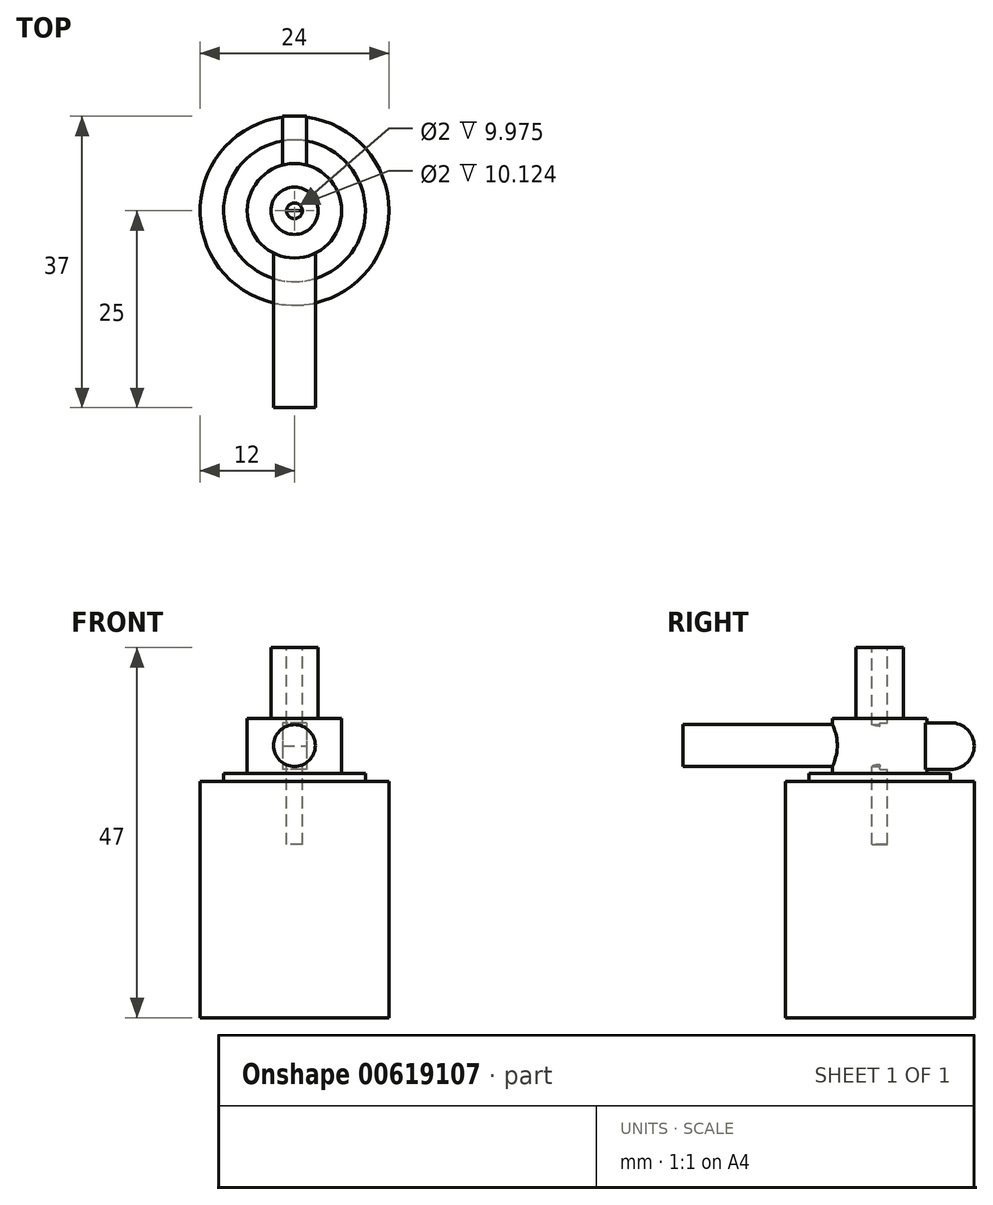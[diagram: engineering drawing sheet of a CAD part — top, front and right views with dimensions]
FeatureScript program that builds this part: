
annotation { "Feature Type Name" : "Feature", "Feature Type Description" : "" }
export const myFeature = defineFeature(function(context is Context, id is Id, definition is map)
    precondition{}
    {
        {
            var Q0;
            Q0=qCreatedBy(makeId("Top.planeOp"),FACE);
            var sketch = newSketch(context, id + "F0", { "sketchPlane" : qUnion([Q0])});
            skCircle(sketch, "E0", {"center": v(0, 0) * mm, "radius": 12 * mm});
            skSolve(sketch);
        }
        {
            var Q0;
            Q0 = qSketchRegion(id + "F0", true);
            extrude(context, id + "F1", {"entities" : qUnion([Q0]), "depth" : 30 * mm, "offsetDistance" : 25 * mm});
        }
        {
            var Q0;
            Q0=makeQuery(id+"F1.opExtrude","CAP_FACE",FACE,{"disambiguationData":[OSD([sQuery(id+"F0.wireOp",EDGE,"E0")])],"isStart":false});
            var sketch = newSketch(context, id + "F2", { "sketchPlane" : qUnion([Q0])});
            skCircle(sketch, "E1", {"center": v(0, 0) * mm, "radius": 9 * mm});
            skSolve(sketch);
        }
        {
            var Q0;
            Q0 = qSketchRegion(id + "F2", true);
            extrude(context, id + "F3", {"entities" : qUnion([Q0]), "operationType" : NewBodyOperationType.ADD, "depth" : 1 * mm, "offsetDistance" : 25 * mm});
        }
        {
            var Q0;
            Q0=makeQuery(id+"F3.opExtrude","CAP_FACE",FACE,{"disambiguationData":[OSD([sQuery(id+"F2.wireOp",EDGE,"E1")])],"isStart":false});
            var sketch = newSketch(context, id + "F4", { "sketchPlane" : qUnion([Q0])});
            skCircle(sketch, "E2", {"center": v(0, 0) * mm, "radius": 6 * mm});
            skSolve(sketch);
        }
        {
            var Q0;
            Q0 = qSketchRegion(id + "F4", true);
            extrude(context, id + "F5", {"entities" : qUnion([Q0]), "operationType" : NewBodyOperationType.ADD, "depth" : 7 * mm, "offsetDistance" : 25 * mm});
        }
        {
            var Q0;
            Q0=makeQuery(id+"F5.opExtrude","CAP_FACE",FACE,{"disambiguationData":[OSD([sQuery(id+"F4.wireOp",EDGE,"E2")])],"isStart":false});
            var sketch = newSketch(context, id + "F6", { "sketchPlane" : qUnion([Q0])});
            skCircle(sketch, "E3", {"center": v(0, 0) * mm, "radius": 3 * mm});
            skSolve(sketch);
        }
        {
            var Q0;
            Q0 = qSketchRegion(id + "F6", true);
            extrude(context, id + "F7", {"entities" : qUnion([Q0]), "operationType" : NewBodyOperationType.ADD, "depth" : 9 * mm, "offsetDistance" : 25 * mm});
        }
        {
            var Q0;
            Q0=makeQuery(id+"F7.opExtrude","CAP_FACE",FACE,{"disambiguationData":[OSD([sQuery(id+"F6.wireOp",EDGE,"E3")])],"isStart":false});
            var sketch = newSketch(context, id + "F8", { "sketchPlane" : qUnion([Q0])});
            skCircle(sketch, "E4", {"center": v(0, 0) * mm, "radius": 1 * mm});
            skSolve(sketch);
        }
        {
            var Q0;
            Q0 = qSketchRegion(id + "F8", true);
            extrude(context, id + "F9", {"entities" : qUnion([Q0]), "operationType" : NewBodyOperationType.REMOVE, "oppositeDirection" : true, "depth" : 25 * mm, "offsetDistance" : 25 * mm});
        }
        {
            var Q0;
            Q0=qCreatedBy(makeId("Front.planeOp"),FACE);
            var sketch = newSketch(context, id + "F10", { "sketchPlane" : qUnion([Q0])});
            skCircle(sketch, "E5", {"center": v(0, 34.57) * mm, "radius": 2.65 * mm});
            skSolve(sketch);
        }
        {
            var Q0;
            Q0 = qSketchRegion(id + "F10", true);
            extrude(context, id + "F11", {"entities" : qUnion([Q0]), "operationType" : NewBodyOperationType.ADD, "depth" : 25 * mm, "offsetDistance" : 25 * mm});
        }
        {
            var Q0;
            Q0=qCreatedBy(makeId("Front.planeOp"),FACE);
            var sketch = newSketch(context, id + "F12", { "sketchPlane" : qUnion([Q0])});
            skLineSegment(sketch, "E6.bottom", {"start": v(1.5, 37.47) * mm, "end": v(-1.5, 37.47) * mm});
            skLineSegment(sketch, "E6.top", {"start": v(1.5, 31.55) * mm, "end": v(-1.5, 31.55) * mm});
            skLineSegment(sketch, "E6.left", {"start": v(1.5, 37.47) * mm, "end": v(1.5, 31.55) * mm});
            skLineSegment(sketch, "E6.right", {"start": v(-1.5, 37.47) * mm, "end": v(-1.5, 31.55) * mm});
            skSolve(sketch);
        }
        {
            var Q0;
            Q0 = qSketchRegion(id + "F12", true);
            extrude(context, id + "F13", {"entities" : qUnion([Q0]), "operationType" : NewBodyOperationType.ADD, "oppositeDirection" : true, "depth" : 12 * mm, "offsetDistance" : 25 * mm});
        }
        {
            var Q0;
            Q0=makeQuery(id+"F13.opExtrude","CAP_EDGE",EDGE,{"disambiguationData":[OSD([sQuery(id+"F12.wireOp",EDGE,"E6.bottom")])],"isStart":false});
            var Q1;
            Q1=makeQuery(id+"F13.opExtrude","CAP_EDGE",EDGE,{"disambiguationData":[OSD([sQuery(id+"F12.wireOp",EDGE,"E6.top")])],"isStart":false});
            fillet(context, id + "F14", {"entities" : qUnion([Q0, Q1]), "radius" : 3 * mm, "tangentPropagation" : true, "allowEdgeOverflow" : false});
        }
    });
